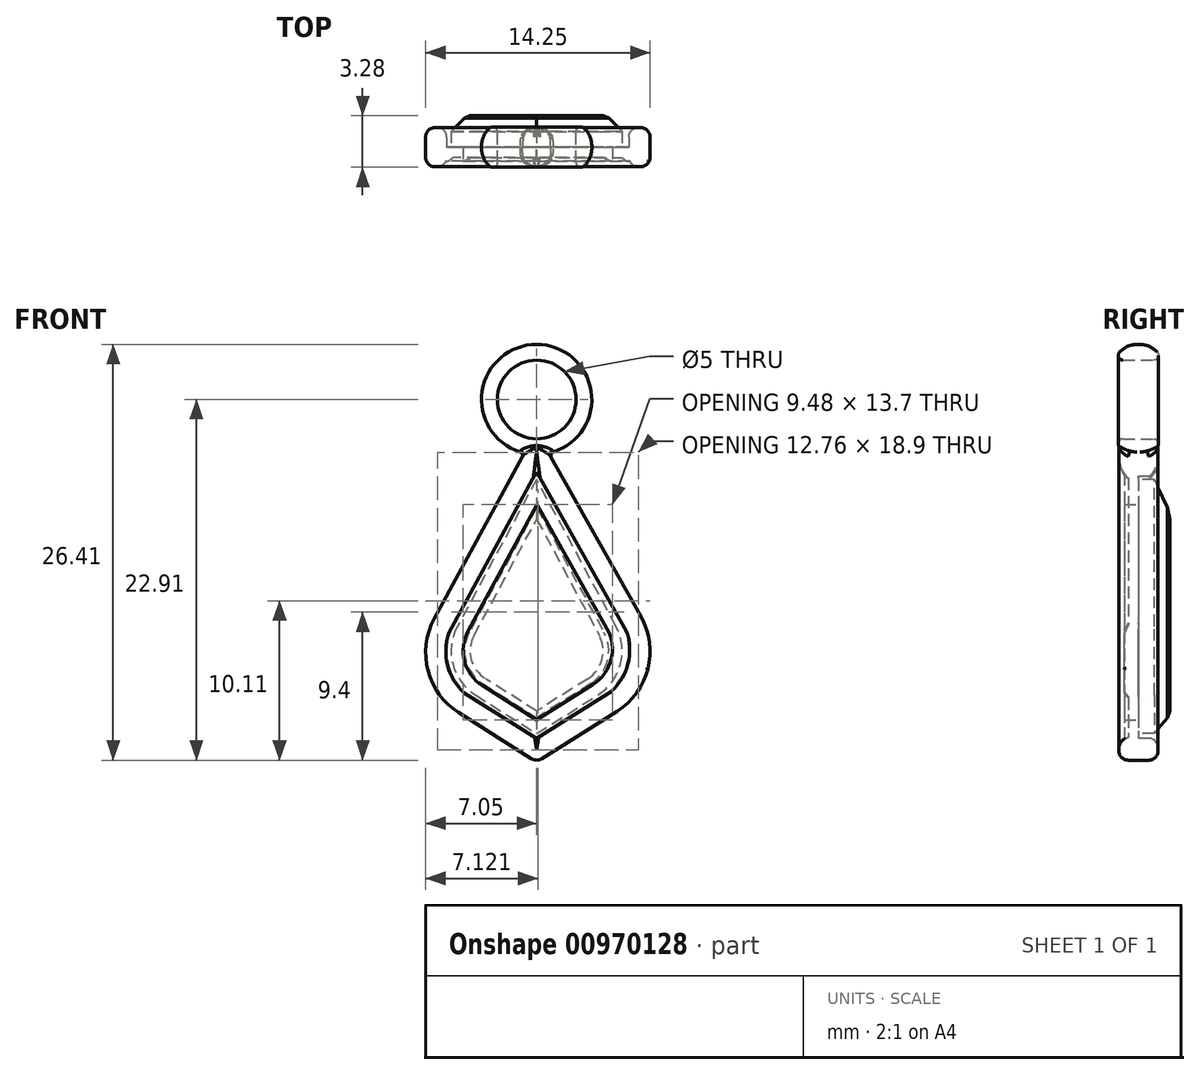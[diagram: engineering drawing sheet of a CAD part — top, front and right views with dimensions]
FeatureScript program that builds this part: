
annotation { "Feature Type Name" : "Feature", "Feature Type Description" : "" }
export const myFeature = defineFeature(function(context is Context, id is Id, definition is map)
    precondition{}
    {
        {
            var Q0;
            Q0=qCreatedBy(makeId("Front.planeOp"),FACE);
            var sketch = newSketch(context, id + "F0", { "sketchPlane" : qUnion([Q0])});
            skCircle(sketch, "E0", {"center": v(0, 12.12) * mm, "radius": 3.5 * mm});
            skCircle(sketch, "E1", {"center": v(0, 12.12) * mm, "radius": 2.5 * mm});
            skSolve(sketch);
        }
        {
            var Q0;
            Q0=makeQuery(id+"F0.imprint","IMPRINT",FACE,{"disambiguationData":[TD([[makeQuery(id+"F0.imprint","IMPRINT",EDGE,{"derivedFrom":sQuery(id+"F0.wireOp",EDGE,"E0")}),1.0]])]});
            extrude(context, id + "F1", {"entities" : qUnion([Q0]), "depth" : 1.5 * mm, "offsetDistance" : 25 * mm, "hasSecondDirection" : true, "secondDirectionOppositeDirection" : true, "secondDirectionDepth" : 1.5 * mm});
        }
        {
            var Q0;
            Q0=makeQuery(id+"F1.opExtrude","CAP_EDGE",EDGE,{"disambiguationData":[OSD([sQuery(id+"F0.wireOp",EDGE,"E0")])],"isStart":true});
            var Q1;
            Q1=makeQuery(id+"F1.opExtrude","CAP_EDGE",EDGE,{"disambiguationData":[OSD([sQuery(id+"F0.wireOp",EDGE,"E0")])],"isStart":false});
            fillet(context, id + "F2", {"entities" : qUnion([Q0, Q1]), "radius" : 1.5 * mm, "tangentPropagation" : true, "allowEdgeOverflow" : false});
        }
        {
            var Q0;
            Q0=makeQuery(id+"F1.opExtrude","SWEPT_FACE",FACE,{"disambiguationData":[OSD([sQuery(id+"F0.wireOp",EDGE,"E1")])]});
            var Q1;
            Q1=makeQuery(id+"F2.opFillet","BLEND_EDGE",EDGE,{"blendedFrom":[makeQuery(id+"F1.opExtrude","CAP_EDGE",EDGE,{"disambiguationData":[OSD([sQuery(id+"F0.wireOp",EDGE,"E0")])],"isStart":true}),makeQuery(id+"F1.opExtrude","SWEPT_FACE",FACE,{"disambiguationData":[OSD([sQuery(id+"F0.wireOp",EDGE,"E1")])]})],"blendedInto":[makeQuery(id+"F1.opExtrude","SWEPT_FACE",FACE,{"disambiguationData":[OSD([sQuery(id+"F0.wireOp",EDGE,"E1")])]})]});
            var Q2;
            Q2=makeQuery(id+"F2.opFillet","BLEND_EDGE",EDGE,{"blendedFrom":[makeQuery(id+"F1.opExtrude","CAP_EDGE",EDGE,{"disambiguationData":[OSD([sQuery(id+"F0.wireOp",EDGE,"E0")])],"isStart":false}),makeQuery(id+"F1.opExtrude","SWEPT_FACE",FACE,{"disambiguationData":[OSD([sQuery(id+"F0.wireOp",EDGE,"E1")])]})],"blendedInto":[makeQuery(id+"F1.opExtrude","SWEPT_FACE",FACE,{"disambiguationData":[OSD([sQuery(id+"F0.wireOp",EDGE,"E1")])]})]});
            fillet(context, id + "F3", {"entities" : qUnion([Q0, Q1, Q2]), "radius" : .3 * mm, "tangentPropagation" : true, "allowEdgeOverflow" : false});
        }
        {
            var Q0;
            Q0=qCreatedBy(makeId("Front.planeOp"),FACE);
            var sketch = newSketch(context, id + "F4", { "sketchPlane" : qUnion([Q0])});
            skLineSegment(sketch, "E2", {"start": v(-0.04, 10.14) * mm, "end": v(8.72, -5.4) * mm});
            skLineSegment(sketch, "E3", {"start": v(8.72, -5.4) * mm, "end": v(0, -10.9) * mm});
            skLineSegment(sketch, "E4.MirrorCS", {"start": v(0, 10.14) * mm, "end": v(-8.52, -5.52) * mm});
            skLineSegment(sketch, "E5.MirrorCS", {"start": v(-8.52, -5.52) * mm, "end": v(0, -10.9) * mm});
            skLineSegment(sketch, "E6.0", {"start": v(0, 7.53) * mm, "end": v(7.04, -4.97) * mm});
            skLineSegment(sketch, "E6.1", {"start": v(0, 7.53) * mm, "end": v(-6.86, -5.09) * mm});
            skLineSegment(sketch, "E6.2", {"start": v(-6.86, -5.09) * mm, "end": v(0, -9.42) * mm});
            skLineSegment(sketch, "E6.3", {"start": v(7.04, -4.97) * mm, "end": v(0, -9.42) * mm});
            skLineSegment(sketch, "E7.0", {"start": v(0.02, 5.46) * mm, "end": v(-5.53, -4.74) * mm});
            skLineSegment(sketch, "E7.1", {"start": v(0.02, 5.46) * mm, "end": v(5.7, -4.63) * mm});
            skLineSegment(sketch, "E7.2", {"start": v(5.7, -4.63) * mm, "end": v(0, -8.24) * mm});
            skLineSegment(sketch, "E7.3", {"start": v(-5.53, -4.74) * mm, "end": v(0, -8.24) * mm});
            skSolve(sketch);
        }
        {
            var Q0;
            Q0=makeQuery(id+"F4.imprint","IMPRINT",FACE,{"disambiguationData":[TD([[makeQuery(id+"F4.imprint","IMPRINT",EDGE,{"derivedFrom":sQuery(id+"F4.wireOp",EDGE,"E2")}),-1.0]])]});
            extrude(context, id + "F5", {"entities" : qUnion([Q0]), "depth" : 1.25 * mm, "offsetDistance" : 25 * mm, "hasSecondDirection" : true, "secondDirectionOppositeDirection" : true, "secondDirectionDepth" : 1.25 * mm});
        }
        {
            var Q0;
            Q0=makeQuery(id+"F5.opExtrude","SWEPT_EDGE",EDGE,{"disambiguationData":[OSD([sQuery(id+"F4.wireOp",EDGE,"E4.MirrorCS"),sQuery(id+"F4.wireOp",EDGE,"E5.MirrorCS")])]});
            var Q1;
            Q1=makeQuery(id+"F5.opExtrude","SWEPT_EDGE",EDGE,{"disambiguationData":[OSD([sQuery(id+"F4.wireOp",EDGE,"E2"),sQuery(id+"F4.wireOp",EDGE,"E3")])]});
            fillet(context, id + "F6", {"entities" : qUnion([Q0, Q1]), "radius" : 4.5 * mm, "tangentPropagation" : true, "allowEdgeOverflow" : false});
        }
        {
            var Q0;
            Q0=makeQuery(id+"F5.opExtrude","SWEPT_EDGE",EDGE,{"disambiguationData":[OSD([sQuery(id+"F4.wireOp",EDGE,"E6.0"),sQuery(id+"F4.wireOp",EDGE,"E6.3")])]});
            var Q1;
            Q1=makeQuery(id+"F5.opExtrude","SWEPT_EDGE",EDGE,{"disambiguationData":[OSD([sQuery(id+"F4.wireOp",EDGE,"E6.1"),sQuery(id+"F4.wireOp",EDGE,"E6.2")])]});
            fillet(context, id + "F7", {"entities" : qUnion([Q0, Q1]), "radius" : 3.5 * mm, "tangentPropagation" : true, "allowEdgeOverflow" : false});
        }
        {
            var Q0;
            {var subQ0=sQuery(id+"F4.wireOp",EDGE,"E3");var subQ1=sQuery(id+"F4.wireOp",EDGE,"E2");Q0=makeQuery(id+"F6.opFillet","BLEND_EDGE",EDGE,{"blendedFrom":[makeQuery(id+"F5.opExtrude","SWEPT_EDGE",EDGE,{"disambiguationData":[OSD([subQ1,subQ0])]}),makeQuery(id+"F5.opExtrude","CAP_FACE",FACE,{"disambiguationData":[OSD([subQ1,subQ0,sQuery(id+"F4.wireOp",EDGE,"E4.MirrorCS"),sQuery(id+"F4.wireOp",EDGE,"E5.MirrorCS"),sQuery(id+"F4.wireOp",EDGE,"E6.0"),sQuery(id+"F4.wireOp",EDGE,"E6.1"),sQuery(id+"F4.wireOp",EDGE,"E6.2"),sQuery(id+"F4.wireOp",EDGE,"E6.3")])],"isStart":false})],"blendedInto":[makeQuery(id+"F5.opExtrude","CAP_FACE",FACE,{"disambiguationData":[OSD([subQ1,subQ0,sQuery(id+"F4.wireOp",EDGE,"E4.MirrorCS"),sQuery(id+"F4.wireOp",EDGE,"E5.MirrorCS"),sQuery(id+"F4.wireOp",EDGE,"E6.0"),sQuery(id+"F4.wireOp",EDGE,"E6.1"),sQuery(id+"F4.wireOp",EDGE,"E6.2"),sQuery(id+"F4.wireOp",EDGE,"E6.3")])],"isStart":false})]});}
            var Q1;
            Q1=makeQuery(id+"F5.opExtrude","CAP_EDGE",EDGE,{"disambiguationData":[OSD([sQuery(id+"F4.wireOp",EDGE,"E3")])],"isStart":false});
            var Q2;
            Q2=makeQuery(id+"F5.opExtrude","CAP_EDGE",EDGE,{"disambiguationData":[OSD([sQuery(id+"F4.wireOp",EDGE,"E6.0")])],"isStart":false});
            var Q3;
            Q3=makeQuery(id+"F5.opExtrude","CAP_EDGE",EDGE,{"disambiguationData":[OSD([sQuery(id+"F4.wireOp",EDGE,"E5.MirrorCS")])],"isStart":false});
            var Q4;
            Q4=makeQuery(id+"F5.opExtrude","CAP_EDGE",EDGE,{"disambiguationData":[OSD([sQuery(id+"F4.wireOp",EDGE,"E6.2")])],"isStart":false});
            var Q5;
            {var subQ0=sQuery(id+"F4.wireOp",EDGE,"E5.MirrorCS");var subQ1=sQuery(id+"F4.wireOp",EDGE,"E4.MirrorCS");Q5=makeQuery(id+"F6.opFillet","BLEND_EDGE",EDGE,{"blendedFrom":[makeQuery(id+"F5.opExtrude","SWEPT_EDGE",EDGE,{"disambiguationData":[OSD([subQ1,subQ0])]}),makeQuery(id+"F5.opExtrude","CAP_FACE",FACE,{"disambiguationData":[OSD([sQuery(id+"F4.wireOp",EDGE,"E2"),sQuery(id+"F4.wireOp",EDGE,"E3"),subQ1,subQ0,sQuery(id+"F4.wireOp",EDGE,"E6.0"),sQuery(id+"F4.wireOp",EDGE,"E6.1"),sQuery(id+"F4.wireOp",EDGE,"E6.2"),sQuery(id+"F4.wireOp",EDGE,"E6.3")])],"isStart":true})],"blendedInto":[makeQuery(id+"F5.opExtrude","CAP_FACE",FACE,{"disambiguationData":[OSD([sQuery(id+"F4.wireOp",EDGE,"E2"),sQuery(id+"F4.wireOp",EDGE,"E3"),subQ1,subQ0,sQuery(id+"F4.wireOp",EDGE,"E6.0"),sQuery(id+"F4.wireOp",EDGE,"E6.1"),sQuery(id+"F4.wireOp",EDGE,"E6.2"),sQuery(id+"F4.wireOp",EDGE,"E6.3")])],"isStart":true})]});}
            var Q6;
            Q6=makeQuery(id+"F5.opExtrude","CAP_EDGE",EDGE,{"disambiguationData":[OSD([sQuery(id+"F4.wireOp",EDGE,"E6.1")])],"isStart":true});
            var Q7;
            Q7=makeQuery(id+"F5.opExtrude","CAP_EDGE",EDGE,{"disambiguationData":[OSD([sQuery(id+"F4.wireOp",EDGE,"E6.0")])],"isStart":true});
            var Q8;
            Q8=makeQuery(id+"F5.opExtrude","CAP_EDGE",EDGE,{"disambiguationData":[OSD([sQuery(id+"F4.wireOp",EDGE,"E3")])],"isStart":true});
            var Q9;
            Q9=makeQuery(id+"F5.opExtrude","SWEPT_EDGE",EDGE,{"disambiguationData":[OSD([sQuery(id+"F4.wireOp",EDGE,"E3"),sQuery(id+"F4.wireOp",EDGE,"E5.MirrorCS")])]});
            fillet(context, id + "F8", {"entities" : qUnion([Q0, Q1, Q2, Q3, Q4, Q5, Q6, Q7, Q8, Q9]), "radius" : .6 * mm, "tangentPropagation" : true, "allowEdgeOverflow" : false});
        }
        {
            var Q0;
            Q0=makeQuery(id+"F8.opFillet","BLEND_EDGE",EDGE,{"blendedFrom":[makeQuery(id+"F5.opExtrude","CAP_EDGE",EDGE,{"disambiguationData":[OSD([sQuery(id+"F4.wireOp",EDGE,"E6.0")])],"isStart":false}),makeQuery(id+"F5.opExtrude","CAP_EDGE",EDGE,{"disambiguationData":[OSD([sQuery(id+"F4.wireOp",EDGE,"E6.1")])],"isStart":false})],"blendedInto":[]});
            var Q1;
            Q1=makeQuery(id+"F5.opExtrude","SWEPT_EDGE",EDGE,{"disambiguationData":[OSD([sQuery(id+"F4.wireOp",EDGE,"E6.2"),sQuery(id+"F4.wireOp",EDGE,"E6.3")])]});
            fillet(context, id + "F9", {"entities" : qUnion([Q0, Q1]), "radius" : .25 * mm, "tangentPropagation" : true, "allowEdgeOverflow" : false});
        }
        {
            var Q0;
            Q0=makeQuery(id+"F5.opExtrude","SWEPT_EDGE",EDGE,{"disambiguationData":[OSD([sQuery(id+"F4.wireOp",EDGE,"E2"),sQuery(id+"F4.wireOp",EDGE,"E4.MirrorCS")])]});
            fillet(context, id + "F10", {"entities" : qUnion([Q0]), "radius" : .5 * mm, "tangentPropagation" : true, "allowEdgeOverflow" : false});
        }
        {
            var Q0;
            Q0=makeQuery(id+"F4.imprint","IMPRINT",FACE,{"disambiguationData":[TD([[makeQuery(id+"F4.imprint","IMPRINT",EDGE,{"derivedFrom":sQuery(id+"F4.wireOp",EDGE,"E6.0")}),-1.0]])]});
            extrude(context, id + "F11", {"entities" : qUnion([Q0]), "depth" : .9 * mm, "offsetDistance" : 25 * mm});
        }
        {
            var Q0;
            Q0=qCreatedBy(makeId("Front.planeOp"),FACE);
            var sketch = newSketch(context, id + "F12", { "sketchPlane" : qUnion([Q0])});
            skLineSegment(sketch, "E8", {"start": v(0, 7.05) * mm, "end": v(-6.5, -5) * mm});
            skLineSegment(sketch, "E9", {"start": v(-6.5, -5) * mm, "end": v(0, -9.1) * mm});
            skLineSegment(sketch, "E10.MirrorCS", {"start": v(6.5, -5) * mm, "end": v(0, -9.1) * mm});
            skLineSegment(sketch, "E11.MirrorCS", {"start": v(0, 7.05) * mm, "end": v(6.5, -5) * mm});
            skSolve(sketch);
        }
        {
            var Q0;
            Q0=qSketchRegion(id+"F12",true);
            extrude(context, id + "F13", {"entities" : qUnion([Q0]), "oppositeDirection" : true, "depth" : 2 * mm, "offsetDistance" : 25 * mm});
        }
        {
            var Q0;
            Q0=makeQuery(id+"F13.opExtrude","SWEPT_EDGE",EDGE,{"disambiguationData":[OSD([sQuery(id+"F12.wireOp",EDGE,"E8"),sQuery(id+"F12.wireOp",EDGE,"E9")])]});
            var Q1;
            Q1=makeQuery(id+"F13.opExtrude","SWEPT_EDGE",EDGE,{"disambiguationData":[OSD([sQuery(id+"F12.wireOp",EDGE,"E10.MirrorCS"),sQuery(id+"F12.wireOp",EDGE,"E11.MirrorCS")])]});
            fillet(context, id + "F14", {"entities" : qUnion([Q0, Q1]), "radius" : 3.3 * mm, "tangentPropagation" : true, "allowEdgeOverflow" : false});
        }
        {
            var Q0;
            Q0=makeQuery(id+"F11.opExtrude","SWEPT_BODY",BODY,{"disambiguationData":[OSD([sQuery(id+"F4.wireOp",EDGE,"E6.0"),sQuery(id+"F4.wireOp",EDGE,"E6.1"),sQuery(id+"F4.wireOp",EDGE,"E6.2"),sQuery(id+"F4.wireOp",EDGE,"E6.3")])]});
            var Q1;
            Q1=makeQuery(id+"F1.opExtrude","SWEPT_BODY",BODY,{"disambiguationData":[OSD([sQuery(id+"F0.wireOp",EDGE,"E0"),sQuery(id+"F0.wireOp",EDGE,"E1")])]});
            var Q2;
            Q2=makeQuery(id+"F5.opExtrude","SWEPT_BODY",BODY,{"disambiguationData":[OSD([sQuery(id+"F4.wireOp",EDGE,"E2"),sQuery(id+"F4.wireOp",EDGE,"E3"),sQuery(id+"F4.wireOp",EDGE,"E4.MirrorCS"),sQuery(id+"F4.wireOp",EDGE,"E5.MirrorCS"),sQuery(id+"F4.wireOp",EDGE,"E6.0"),sQuery(id+"F4.wireOp",EDGE,"E6.1"),sQuery(id+"F4.wireOp",EDGE,"E6.2"),sQuery(id+"F4.wireOp",EDGE,"E6.3")])]});
            booleanBodies(context, id + "F15", {"operationType" : BooleanOperationType.UNION, "tools" : qUnion([Q0, Q1, Q2])});
        }
        {
            var Q0;
            {var subQ0=sQuery(id+"F0.wireOp",EDGE,"E0");Q0=makeQuery(id+"F15.opBoolean","INTERSECT",EDGE,{"derivedFrom":[makeQuery(id+"F2.opFillet","BLEND_FACE",FACE,{"disambiguationData":[OSD([subQ0]),TDD([makeQuery(id+"F1.opExtrude","CAP_EDGE",EDGE,{"disambiguationData":[OSD([subQ0])],"isStart":false})])]}),makeQuery(id+"F5.opExtrude","SWEPT_FACE",FACE,{"disambiguationData":[OSD([sQuery(id+"F4.wireOp",EDGE,"E2")])]})]});}
            fillet(context, id + "F16", {"entities" : qUnion([Q0]), "radius" : .25 * mm, "tangentPropagation" : true, "allowEdgeOverflow" : false});
        }
        {
            var Q0;
            Q0=makeQuery(id+"F11.opExtrude","SWEPT_EDGE",EDGE,{"disambiguationData":[OSD([sQuery(id+"F4.wireOp",EDGE,"E7.0"),sQuery(id+"F4.wireOp",EDGE,"E7.3")])]});
            var Q1;
            Q1=makeQuery(id+"F11.opExtrude","SWEPT_EDGE",EDGE,{"disambiguationData":[OSD([sQuery(id+"F4.wireOp",EDGE,"E7.1"),sQuery(id+"F4.wireOp",EDGE,"E7.2")])]});
            fillet(context, id + "F17", {"entities" : qUnion([Q0, Q1]), "radius" : 2.63 * mm, "tangentPropagation" : true, "allowEdgeOverflow" : false});
        }
        {
            var Q0;
            Q0=makeQuery(id+"F13.opExtrude","CAP_FACE",FACE,{"disambiguationData":[OSD([sQuery(id+"F12.wireOp",EDGE,"E8"),sQuery(id+"F12.wireOp",EDGE,"E9"),sQuery(id+"F12.wireOp",EDGE,"E10.MirrorCS"),sQuery(id+"F12.wireOp",EDGE,"E11.MirrorCS")])],"isStart":false});
            chamfer(context, id + "F18", {"entities" : qUnion([Q0]), "width" : 1 * mm, "tangentPropagation" : true});
        }
        {
            var Q0;
            Q0=makeQuery(id+"F13.opExtrude","CAP_FACE",FACE,{"disambiguationData":[OSD([sQuery(id+"F12.wireOp",EDGE,"E8"),sQuery(id+"F12.wireOp",EDGE,"E9"),sQuery(id+"F12.wireOp",EDGE,"E10.MirrorCS"),sQuery(id+"F12.wireOp",EDGE,"E11.MirrorCS")])],"isStart":false});
            chamfer(context, id + "F19", {"entities" : qUnion([Q0]), "width" : .5 * mm, "tangentPropagation" : true});
        }
    });
